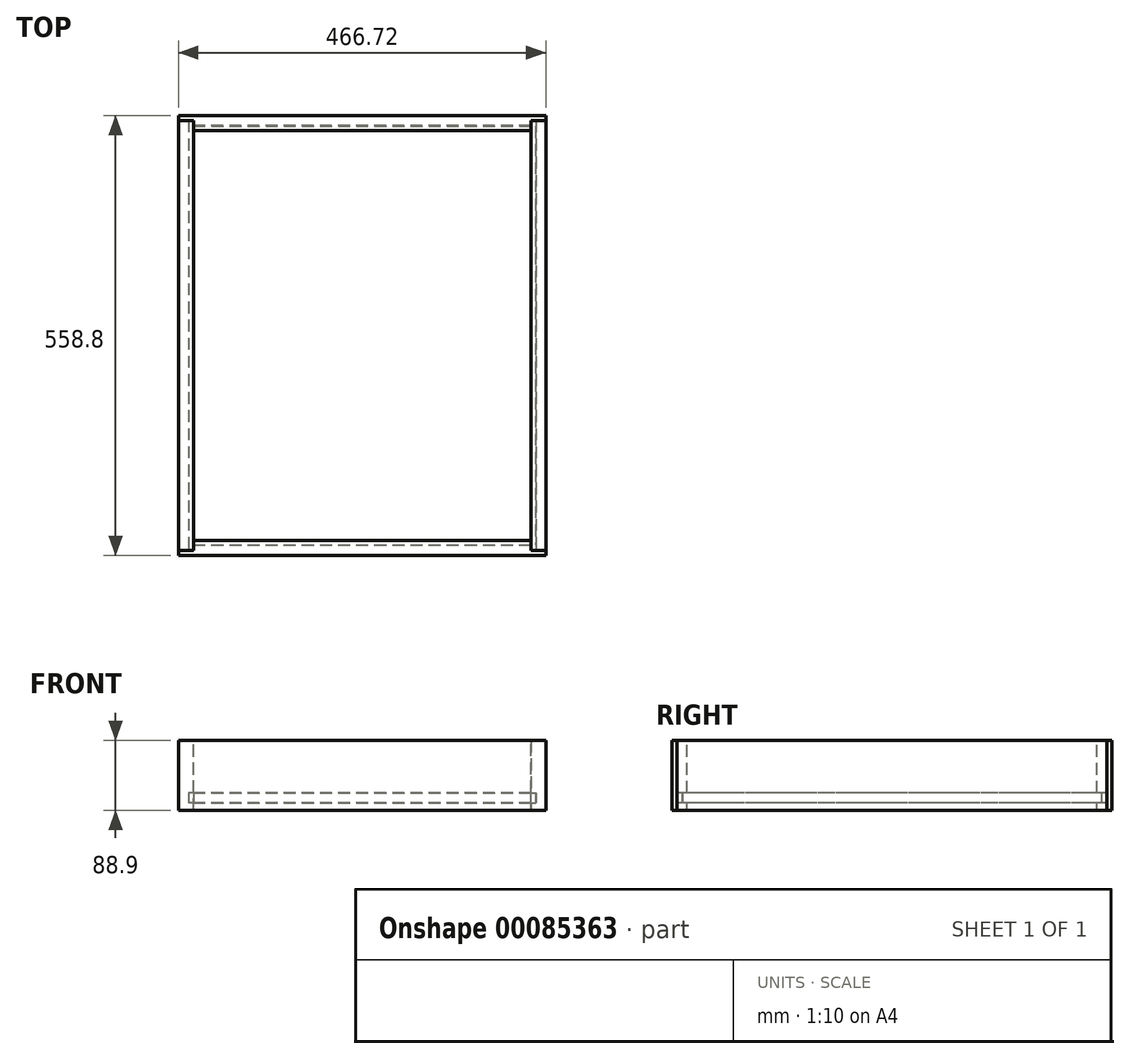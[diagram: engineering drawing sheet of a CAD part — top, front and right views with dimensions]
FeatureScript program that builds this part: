
annotation { "Feature Type Name" : "Feature", "Feature Type Description" : "" }
export const myFeature = defineFeature(function(context is Context, id is Id, definition is map)
    precondition{}
    {
        {
            var Q0;
            Q0=qCreatedBy(makeId("Front.planeOp"),FACE);
            var sketch = newSketch(context, id + "F0", { "sketchPlane" : qUnion([Q0])});
            skLineSegment(sketch, "E0.bottom", {"start": v(233.36, 0) * mm, "end": v(-233.36, 0) * mm, "construction": true});
            skLineSegment(sketch, "E0.top", {"start": v(233.36, 88.9) * mm, "end": v(-233.36, 88.9) * mm, "construction": true});
            skLineSegment(sketch, "E0.left", {"start": v(233.36, 0) * mm, "end": v(233.36, 88.9) * mm, "construction": true});
            skLineSegment(sketch, "E0.right", {"start": v(-233.36, 0) * mm, "end": v(-233.36, 88.9) * mm, "construction": true});
            skPoint(sketch, "E0.middle", {"position": v(0, 44.45) * mm});
            skLineSegment(sketch, "E1.bottom", {"start": v(-233.36, 88.9) * mm, "end": v(-214.31, 88.9) * mm});
            skLineSegment(sketch, "E1.top", {"start": v(-233.36, 0) * mm, "end": v(-214.31, 0) * mm});
            skLineSegment(sketch, "E1.left", {"start": v(-233.36, 88.9) * mm, "end": v(-233.36, 0) * mm});
            skLineSegment(sketch, "E1.right", {"start": v(-214.31, 88.9) * mm, "end": v(-214.31, 0) * mm});
            skLineSegment(sketch, "E2", {"start": v(0, 0) * mm, "end": v(0, 88.9) * mm, "construction": true});
            skSolve(sketch);
        }
        {
            var Q0;
            Q0=makeQuery(id+"F0.imprint","IMPRINT",FACE,{"disambiguationData":[TD([[makeQuery(id+"F0.imprint","IMPRINT",EDGE,{"derivedFrom":sQuery(id+"F0.wireOp",EDGE,"E1.bottom")}),-1.0]])]});
            extrude(context, id + "F1", {"entities" : qUnion([Q0]), "endBound" : BoundingType.SYMMETRIC, "depth" : 546.1 * mm});
        }
        {
            var Q0;
            Q0=makeQuery(id+"F1.opExtrude","CAP_FACE",FACE,{"disambiguationData":[OSD([sQuery(id+"F0.wireOp",EDGE,"E1.bottom"),sQuery(id+"F0.wireOp",EDGE,"E1.top"),sQuery(id+"F0.wireOp",EDGE,"E1.left"),sQuery(id+"F0.wireOp",EDGE,"E1.right")])],"isStart":false});
            var sketch = newSketch(context, id + "F2", { "sketchPlane" : qUnion([Q0])});
            skLineSegment(sketch, "E3.bottom", {"start": v(-214.31, 22.22) * mm, "end": v(-220.66, 22.22) * mm});
            skLineSegment(sketch, "E3.top", {"start": v(-214.31, 9.52) * mm, "end": v(-220.66, 9.52) * mm});
            skLineSegment(sketch, "E3.left", {"start": v(-214.31, 22.22) * mm, "end": v(-214.31, 9.52) * mm});
            skLineSegment(sketch, "E3.right", {"start": v(-220.66, 22.22) * mm, "end": v(-220.66, 9.52) * mm});
            skSolve(sketch);
        }
        {
            var Q0;
            Q0=makeQuery(id+"F2.imprint","IMPRINT",FACE,{"disambiguationData":[TD([[makeQuery(id+"F2.imprint","IMPRINT",EDGE,{"derivedFrom":sQuery(id+"F2.wireOp",EDGE,"E3.bottom")}),1.0]])]});
            extrude(context, id + "F3", {"entities" : qUnion([Q0]), "operationType" : NewBodyOperationType.REMOVE, "endBound" : BoundingType.THROUGH_ALL, "oppositeDirection" : true, "depth" : 25.4 * mm});
        }
        {
            var Q0;
            Q0=makeQuery(id+"F1.opExtrude","SWEPT_BODY",BODY,{"disambiguationData":[OSD([sQuery(id+"F0.wireOp",EDGE,"E1.bottom"),sQuery(id+"F0.wireOp",EDGE,"E1.top"),sQuery(id+"F0.wireOp",EDGE,"E1.left"),sQuery(id+"F0.wireOp",EDGE,"E1.right")])]});
            var Q1;
            Q1=qCreatedBy(makeId("Right.planeOp"),FACE);
            mirror(context, id + "F4", {"entities" : qUnion([Q0]), "mirrorPlane" : qUnion([Q1])});
        }
        {
            var Q0;
            Q0=makeQuery(id+"F1.opExtrude","SWEPT_FACE",FACE,{"disambiguationData":[OSD([sQuery(id+"F0.wireOp",EDGE,"E1.bottom")])]});
            var sketch = newSketch(context, id + "F5", { "sketchPlane" : qUnion([Q0])});
            skLineSegment(sketch, "E4", {"start": v(-214.31, -260.35) * mm, "end": v(-214.31, -273.05) * mm});
            skLineSegment(sketch, "E5", {"start": v(-214.31, -273.05) * mm, "end": v(-233.36, -273.05) * mm});
            skLineSegment(sketch, "E6", {"start": v(-233.36, -273.05) * mm, "end": v(-233.36, -279.4) * mm});
            skLineSegment(sketch, "E7", {"start": v(-233.36, -279.4) * mm, "end": v(233.36, -279.4) * mm});
            skLineSegment(sketch, "E8", {"start": v(-214.31, -260.35) * mm, "end": v(214.31, -260.35) * mm});
            skLineSegment(sketch, "E9", {"start": v(214.31, -260.35) * mm, "end": v(214.31, -273.05) * mm});
            skLineSegment(sketch, "E10", {"start": v(214.31, -273.05) * mm, "end": v(233.36, -273.05) * mm});
            skLineSegment(sketch, "E11", {"start": v(233.36, -273.05) * mm, "end": v(233.36, -279.4) * mm});
            skSolve(sketch);
        }
        {
            var Q0;
            Q0=makeQuery(id+"F5.imprint","IMPRINT",FACE,{"disambiguationData":[TD([[makeQuery(id+"F5.imprint","IMPRINT",EDGE,{"derivedFrom":sQuery(id+"F5.wireOp",EDGE,"E4")}),-1.0]])]});
            var Q1;
            Q1=makeQuery(id+"F1.opExtrude","SWEPT_FACE",FACE,{"disambiguationData":[OSD([sQuery(id+"F0.wireOp",EDGE,"E1.top")])]});
            extrude(context, id + "F6", {"entities" : qUnion([Q0]), "endBound" : BoundingType.UP_TO_SURFACE, "oppositeDirection" : true, "endBoundEntityFace" : qUnion([Q1]), "depth" : 25.4 * mm});
        }
        {
            var Q0;
            Q0=makeQuery(id+"F6.opExtrude","SWEPT_FACE",FACE,{"disambiguationData":[OSD([sQuery(id+"F5.wireOp",EDGE,"E4")])]});
            var sketch = newSketch(context, id + "F7", { "sketchPlane" : qUnion([Q0])});
            skLineSegment(sketch, "E12.bottom", {"start": v(260.35, 22.22) * mm, "end": v(266.7, 22.22) * mm});
            skLineSegment(sketch, "E12.top", {"start": v(260.35, 9.52) * mm, "end": v(266.7, 9.52) * mm});
            skLineSegment(sketch, "E12.left", {"start": v(260.35, 22.22) * mm, "end": v(260.35, 9.52) * mm});
            skLineSegment(sketch, "E12.right", {"start": v(266.7, 22.22) * mm, "end": v(266.7, 9.52) * mm});
            skSolve(sketch);
        }
        {
            var Q0;
            Q0=makeQuery(id+"F7.imprint","IMPRINT",FACE,{"disambiguationData":[TD([[makeQuery(id+"F7.imprint","IMPRINT",EDGE,{"derivedFrom":sQuery(id+"F7.wireOp",EDGE,"E12.bottom")}),-1.0]])]});
            extrude(context, id + "F8", {"entities" : qUnion([Q0]), "operationType" : NewBodyOperationType.REMOVE, "endBound" : BoundingType.UP_TO_NEXT, "oppositeDirection" : true, "depth" : 25.4 * mm});
        }
        {
            var Q0;
            Q0=makeQuery(id+"F6.opExtrude","SWEPT_BODY",BODY,{"disambiguationData":[OSD([sQuery(id+"F5.wireOp",EDGE,"E4"),sQuery(id+"F5.wireOp",EDGE,"E5"),sQuery(id+"F5.wireOp",EDGE,"E6"),sQuery(id+"F5.wireOp",EDGE,"E7"),sQuery(id+"F5.wireOp",EDGE,"E8"),sQuery(id+"F5.wireOp",EDGE,"E9"),sQuery(id+"F5.wireOp",EDGE,"E10"),sQuery(id+"F5.wireOp",EDGE,"E11")])]});
            var Q1;
            Q1=qCreatedBy(makeId("Front.planeOp"),FACE);
            mirror(context, id + "F9", {"entities" : qUnion([Q0]), "mirrorPlane" : qUnion([Q1])});
        }
        {
            var Q0;
            Q0=makeQuery(id+"F3.boolean.opBoolean","COPY",FACE,{"derivedFrom":makeQuery(id+"F3.opExtrude","SWEPT_FACE",FACE,{"disambiguationData":[OSD([sQuery(id+"F2.wireOp",EDGE,"E3.top")])]})});
            var sketch = newSketch(context, id + "F10", { "sketchPlane" : qUnion([Q0])});
            skLineSegment(sketch, "E13.bottom", {"start": v(-219.9, 265.94) * mm, "end": v(219.9, 265.94) * mm});
            skLineSegment(sketch, "E13.top", {"start": v(-219.9, -265.94) * mm, "end": v(219.9, -265.94) * mm});
            skLineSegment(sketch, "E13.left", {"start": v(-219.9, 265.94) * mm, "end": v(-219.9, -265.94) * mm});
            skLineSegment(sketch, "E13.right", {"start": v(219.9, 265.94) * mm, "end": v(219.9, -265.94) * mm});
            skSolve(sketch);
        }
        {
            var Q0;
            {var subQ0=sQuery(id+"F10.wireOp",EDGE,"E13.right");Q0=makeQuery(id+"F10.imprint","IMPRINT",FACE,{"disambiguationData":[TD([[makeQuery(id+"F10.imprint","IMPRINT",EDGE,{"derivedFrom":subQ0}),-1.0]])]});}
            extrude(context, id + "F11", {"entities" : qUnion([Q0]), "depth" : 12.7 * mm});
        }
    });
